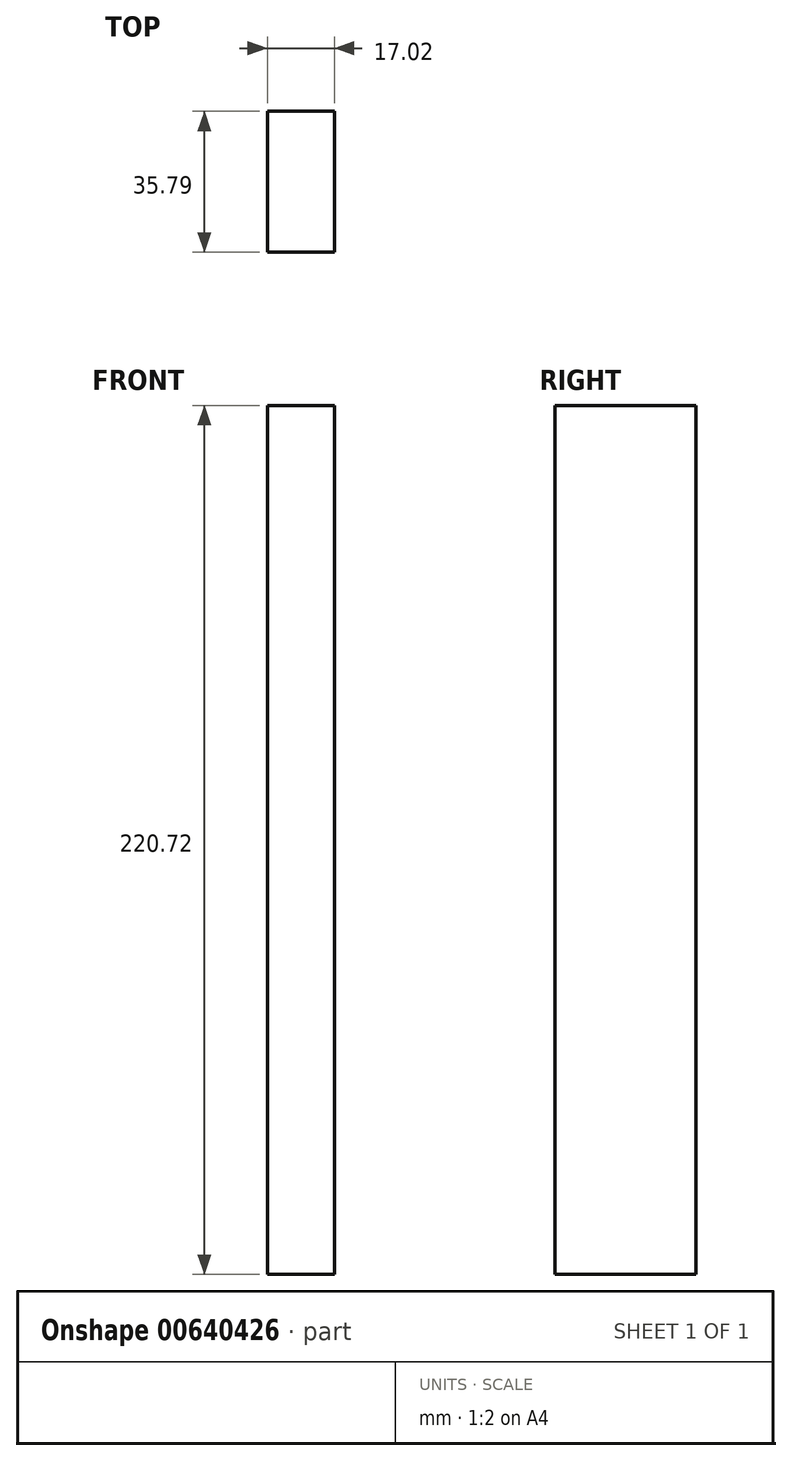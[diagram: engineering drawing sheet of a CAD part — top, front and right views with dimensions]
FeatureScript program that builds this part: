
annotation { "Feature Type Name" : "Feature", "Feature Type Description" : "" }
export const myFeature = defineFeature(function(context is Context, id is Id, definition is map)
    precondition{}
    {
        {
            var Q0;
            Q0=qCreatedBy(makeId("Top.planeOp"),FACE);
            var sketch = newSketch(context, id + "F0", { "sketchPlane" : qUnion([Q0])});
            skCircle(sketch, "E0", {"center": v(0, -18.82) * mm, "radius": 8.18 * mm});
            skLineSegment(sketch, "E1.bottom", {"start": v(-8.63, 0) * mm, "end": v(8.39, 0) * mm});
            skLineSegment(sketch, "E1.top", {"start": v(-8.63, -35.8) * mm, "end": v(8.39, -35.8) * mm});
            skLineSegment(sketch, "E1.left", {"start": v(-8.63, 0) * mm, "end": v(-8.63, -35.8) * mm});
            skLineSegment(sketch, "E1.right", {"start": v(8.39, 0) * mm, "end": v(8.39, -35.8) * mm});
            skSolve(sketch);
        }
        {
            var Q0;
            Q0=makeQuery(id+"F0.imprint","IMPRINT",FACE,{"disambiguationData":[TD([[makeQuery(id+"F0.imprint","IMPRINT",EDGE,{"derivedFrom":sQuery(id+"F0.wireOp",EDGE,"E0")}),-1.0]])]});
            var Q1;
            Q1=makeQuery(id+"F0.imprint","IMPRINT",FACE,{"disambiguationData":[TD([[makeQuery(id+"F0.imprint","IMPRINT",EDGE,{"derivedFrom":sQuery(id+"F0.wireOp",EDGE,"E0")}),1.0]])]});
            extrude(context, id + "F1", {"entities" : qUnion([Q0, Q1]), "oppositeDirection" : true, "depth" : 109.98 * mm, "offsetDistance" : 25.4 * mm});
        }
        {
            var Q0;
            Q0=makeQuery(id+"F1.opExtrude","CAP_FACE",FACE,{"disambiguationData":[OSD([sQuery(id+"F0.wireOp",EDGE,"E1.bottom"),sQuery(id+"F0.wireOp",EDGE,"E1.top"),sQuery(id+"F0.wireOp",EDGE,"E1.left"),sQuery(id+"F0.wireOp",EDGE,"E1.right")])],"isStart":true});
            extrude(context, id + "F2", {"entities" : qUnion([Q0]), "operationType" : NewBodyOperationType.ADD, "depth" : 110.74 * mm, "offsetDistance" : 25.4 * mm});
        }
    });
